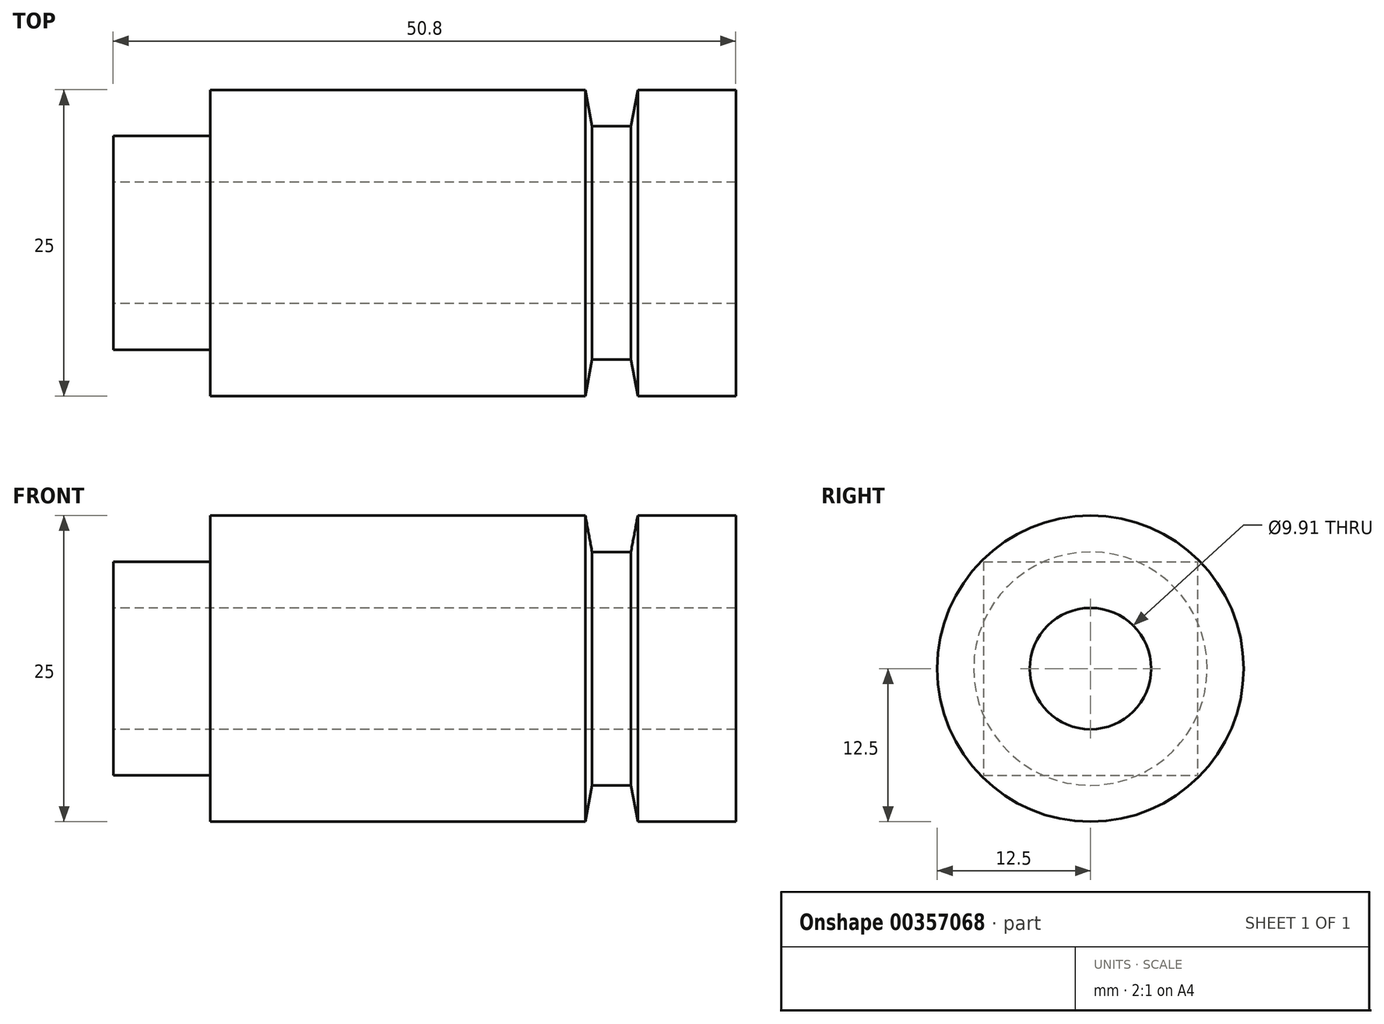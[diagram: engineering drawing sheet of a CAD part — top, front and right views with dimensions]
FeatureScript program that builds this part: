
annotation { "Feature Type Name" : "Feature", "Feature Type Description" : "" }
export const myFeature = defineFeature(function(context is Context, id is Id, definition is map)
    precondition{}
    {
        {
            var Q0;
            Q0=qCreatedBy(makeId("Front.planeOp"),FACE);
            var sketch = newSketch(context, id + "F0", { "sketchPlane" : qUnion([Q0])});
            skLineSegment(sketch, "E0", {"start": v(-102.35, 0) * mm, "end": v(106.3, 0) * mm, "construction": true});
            skLineSegment(sketch, "E1", {"start": v(1.12, 4.95) * mm, "end": v(44, 4.95) * mm});
            skLineSegment(sketch, "E2", {"start": v(44, 4.95) * mm, "end": v(44, 12.5) * mm});
            skLineSegment(sketch, "E3", {"start": v(44, 12.5) * mm, "end": v(36, 12.5) * mm});
            skLineSegment(sketch, "E4", {"start": v(36, 12.5) * mm, "end": v(35.44, 9.53) * mm});
            skLineSegment(sketch, "E5", {"start": v(35.44, 9.53) * mm, "end": v(32.27, 9.53) * mm});
            skLineSegment(sketch, "E6", {"start": v(32.27, 9.53) * mm, "end": v(31.72, 12.5) * mm});
            skLineSegment(sketch, "E7", {"start": v(31.72, 12.5) * mm, "end": v(1.12, 12.5) * mm});
            skLineSegment(sketch, "E8", {"start": v(1.12, 12.5) * mm, "end": v(1.12, 4.95) * mm});
            skLineSegment(sketch, "E9", {"start": v(1.12, 9.53) * mm, "end": v(-6.8, 9.53) * mm});
            skLineSegment(sketch, "E10", {"start": v(-6.8, 9.53) * mm, "end": v(-6.8, 4.95) * mm});
            skLineSegment(sketch, "E11", {"start": v(-6.8, 4.95) * mm, "end": v(1.12, 4.95) * mm});
            skSolve(sketch);
        }
        {
            var Q0;
            Q0=makeQuery(id+"F0.imprint","IMPRINT",FACE,{"disambiguationData":[TD([[makeQuery(id+"F0.imprint","IMPRINT",EDGE,{"derivedFrom":sQuery(id+"F0.wireOp",EDGE,"E1")}),1.0]])]});
            var Q1;
            Q1=sQuery(id+"F0.wireOp",EDGE,"E0");
            revolve(context, id + "F1", {"entities" : qUnion([Q0]), "axis" : qUnion([Q1]), "revolveType" : RevolveType.FULL});
        }
        {
            var Q0;
            Q0=makeQuery(id+"F1.opRevolve","SWEPT_FACE",FACE,{"disambiguationData":[OSD([sQuery(id+"F0.wireOp",EDGE,"E8")])]});
            var sketch = newSketch(context, id + "F2", { "sketchPlane" : qUnion([Q0])});
            skLineSegment(sketch, "E12.bottom", {"start": v(8.72, 8.72) * mm, "end": v(-8.72, 8.72) * mm});
            skLineSegment(sketch, "E12.top", {"start": v(8.72, -8.72) * mm, "end": v(-8.72, -8.72) * mm});
            skLineSegment(sketch, "E12.left", {"start": v(8.72, 8.72) * mm, "end": v(8.72, -8.72) * mm});
            skLineSegment(sketch, "E12.right", {"start": v(-8.72, 8.72) * mm, "end": v(-8.72, -8.72) * mm});
            skPoint(sketch, "E12.middle", {"position": v(0, 0) * mm});
            skSolve(sketch);
        }
        {
            var Q0;
            Q0=makeQuery(id+"F2.imprint","IMPRINT",FACE,{"disambiguationData":[TD([[makeQuery(id+"F2.imprint","IMPRINT",EDGE,{"derivedFrom":sQuery(id+"F2.wireOp",EDGE,"E12.bottom")}),1.0]])]});
            extrude(context, id + "F3", {"entities" : qUnion([Q0]), "operationType" : NewBodyOperationType.ADD, "depth" : 7.92 * mm});
        }
    });
